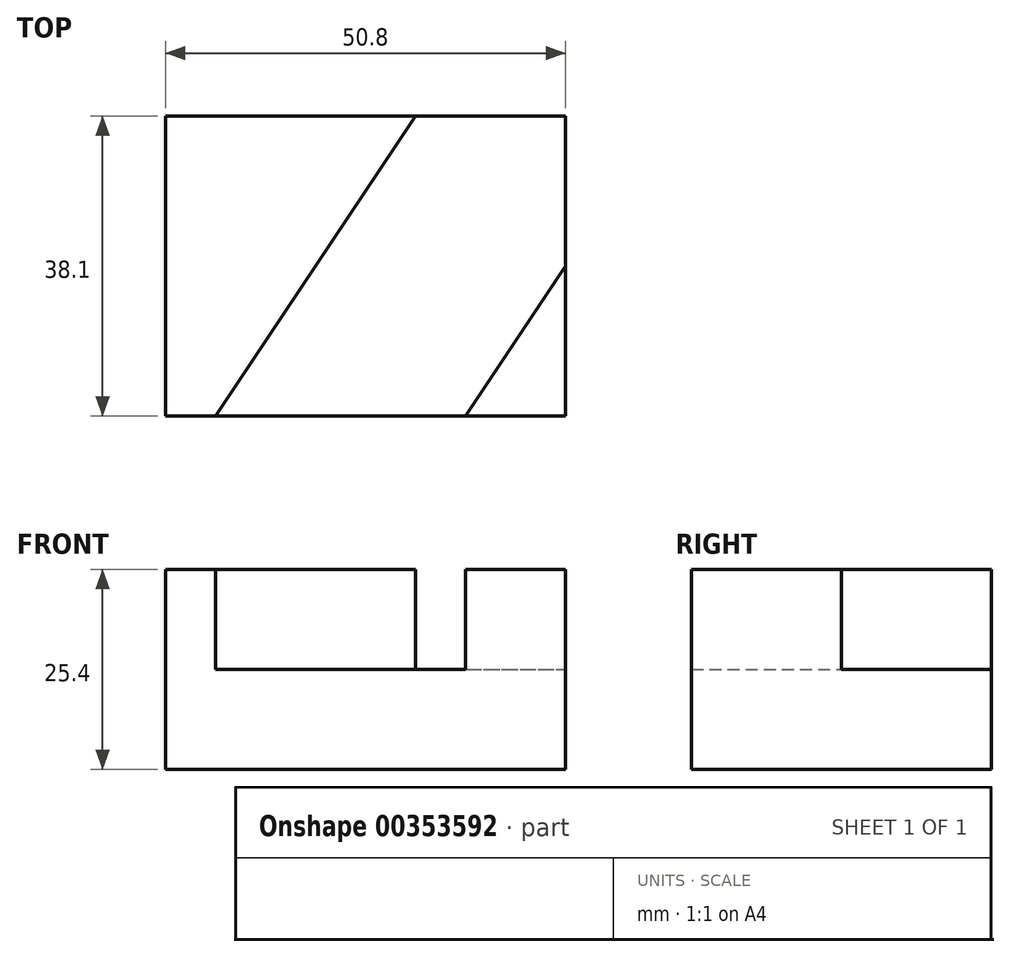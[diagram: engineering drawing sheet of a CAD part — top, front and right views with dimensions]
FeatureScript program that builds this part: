
annotation { "Feature Type Name" : "Feature", "Feature Type Description" : "" }
export const myFeature = defineFeature(function(context is Context, id is Id, definition is map)
    precondition{}
    {
        {
            var Q0;
            Q0=qCreatedBy(makeId("Top.planeOp"),FACE);
            var sketch = newSketch(context, id + "F0", { "sketchPlane" : qUnion([Q0])});
            skLineSegment(sketch, "E0", {"start": v(0, 0) * mm, "end": v(0, 38.1) * mm});
            skLineSegment(sketch, "E1", {"start": v(0, 38.1) * mm, "end": v(50.8, 38.1) * mm});
            skLineSegment(sketch, "E2", {"start": v(50.8, 38.1) * mm, "end": v(50.8, 0) * mm});
            skLineSegment(sketch, "E3", {"start": v(50.8, 0) * mm, "end": v(0, 0) * mm});
            skSolve(sketch);
        }
        {
            var Q0;
            Q0=makeQuery(id+"F0.imprint","IMPRINT",FACE,{"disambiguationData":[TD([[makeQuery(id+"F0.imprint","IMPRINT",EDGE,{"derivedFrom":sQuery(id+"F0.wireOp",EDGE,"E0")}),-1.0]])]});
            extrude(context, id + "F1", {"entities" : qUnion([Q0]), "depth" : 12.7 * mm});
        }
        {
            var Q0;
            Q0=makeQuery(id+"F1.opExtrude","CAP_FACE",FACE,{"disambiguationData":[OSD([sQuery(id+"F0.wireOp",EDGE,"E0"),sQuery(id+"F0.wireOp",EDGE,"E1"),sQuery(id+"F0.wireOp",EDGE,"E2"),sQuery(id+"F0.wireOp",EDGE,"E3")])],"isStart":false});
            var sketch = newSketch(context, id + "F2", { "sketchPlane" : qUnion([Q0])});
            skLineSegment(sketch, "E4", {"start": v(6.35, 0) * mm, "end": v(31.75, 38.1) * mm});
            skLineSegment(sketch, "E5", {"start": v(31.75, 38.1) * mm, "end": v(0, 38.1) * mm});
            skLineSegment(sketch, "E6", {"start": v(0, 38.1) * mm, "end": v(0, 0) * mm});
            skLineSegment(sketch, "E7", {"start": v(0, 0) * mm, "end": v(6.35, 0) * mm});
            skSolve(sketch);
        }
        {
            var Q0;
            {var subQ0=sQuery(id+"F2.wireOp",EDGE,"E4");Q0=makeQuery(id+"F2.imprint","IMPRINT",FACE,{"disambiguationData":[TD([[makeQuery(id+"F2.imprint","IMPRINT",EDGE,{"derivedFrom":subQ0}),-1.0]])]});}
            var sketch = newSketch(context, id + "F3", { "sketchPlane" : qUnion([Q0])});
            skSolve(sketch);
        }
        {
            var Q0;
            Q0=makeQuery(id+"F2.imprint","IMPRINT",FACE,{"disambiguationData":[TD([[makeQuery(id+"F2.imprint","IMPRINT",EDGE,{"derivedFrom":sQuery(id+"F2.wireOp",EDGE,"E4")}),1.0]])]});
            extrude(context, id + "F4", {"entities" : qUnion([Q0]), "operationType" : NewBodyOperationType.ADD, "depth" : 12.7 * mm});
        }
        {
            var Q0;
            {var subQ0=sQuery(id+"F2.wireOp",EDGE,"E4");Q0=makeQuery(id+"F3.imprint","IMPRINT",FACE,{"disambiguationData":[TD([[makeQuery(id+"F3.imprint","IMPRINT",EDGE,{"derivedFrom":makeQuery(id+"F2.imprint","IMPRINT",EDGE,{"derivedFrom":subQ0})}),-1.0]])]});}
            var sketch = newSketch(context, id + "F5", { "sketchPlane" : qUnion([Q0])});
            skLineSegment(sketch, "E8", {"start": v(38.1, 0) * mm, "end": v(50.8, 19.05) * mm});
            skLineSegment(sketch, "E9", {"start": v(50.8, 19.05) * mm, "end": v(50.8, 0) * mm});
            skLineSegment(sketch, "E10", {"start": v(38.1, 0) * mm, "end": v(50.8, 0) * mm});
            skSolve(sketch);
        }
        {
            var Q0;
            Q0 = qSketchRegion(id + "F5", true);
            extrude(context, id + "F6", {"entities" : qUnion([Q0]), "operationType" : NewBodyOperationType.ADD, "depth" : 12.7 * mm});
        }
    });
